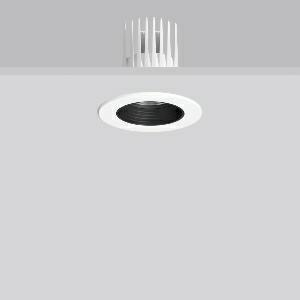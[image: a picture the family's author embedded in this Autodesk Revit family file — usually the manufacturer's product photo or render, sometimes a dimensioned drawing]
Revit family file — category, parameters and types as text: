
# Revit family: heledon_mini_e_901745_002_2_76_e601
name_source: partatom
category: Lighting Fixtures
units: mm (PartAtom-declared; Revit-internal decimal feet)

## family parameters
Cut with Voids When Loaded = No
Host = Face
Light Source = No
Part Type = Normal
Room Calculation Point = No
Round Connector Dimension = Use Diameter
Shared = No

## types (1)
- HELEDON mini E (1 x LED Modul 927, 1900 lm, 2700)
    Apparent Load = 20 VA
    Approval mark = CE
    CIE Flux Codes = 98 100 100 100 100
    Color Rendering = 92
    Color Temperature = 2700
    Default Elevation = 1800 mm
    Description = Series: HELEDON mini
Round recessed downlight. Housing: die-cast aluminium, powder-coated. Black plastic ring and recessed LED to prevent glare from the side. Optical assembly with lens made of plastic (polycarbonate) for the best homogeneous light distribution - can be changed without tools. Best colour rendering index Ra>90. Suitable for Recessed ceiling mounting. Installation without tools thanks to spring fastening system. Including separate LED converter with connecting cable 600 mm.High quality converter without flickering and stroboscopic effect. Through-wiring box (5 pole) available as accessory. The following accessories can be mounted without use of tools: interchangeable lenses, decorative glasses, honeycomb louvre, clear and frosted diffusers, white interchangeable plastic ring. 
Colour: traffic white, matt (RAL 9016)
Diameter: 124 mm
Height: 3 mm
Cut-out diameter: 114 mm
Recess height: 170 mm
Luminaire: recess height: 120 mm
Lamp: LED
Socket: without socket
Colour temperature: 2700K
Colour rendering index (CRI): 92
System power: 20 W
Rated luminous flux: 1900 lm
Luminous efficiency: 95 lm/W
Control gear: Converter, dimmable, DALI
Protection class: II
Type of protection: IP 20
    Height = 0 mm  [stored 0 ft]
    Lamp = 1 x LED Modul 927
    Lamp Light Flux = 1900 lm
    Lamp count = 1
    Length = 124 mm  [stored 0.406824 ft]
    Lifetime = 50000 h
    Luminous efficacy = 95 lm/W
    Manufacturer = RZB
    ModVariant = No
    Model = 901745.002.2.76
    Mounting Place = Ceiling
    Mounting Type = Recessed
    Number of Poles = 1
    OnlyDefault = Yes
    Power Factor = 1
    Product Name = HELEDON mini E
    Product group = Recessed downlights
    ProductGroupID = 402
    Protection Class = Protection class II
    Protection Degree = IP 20
    RLX_Detail_Level = 1
    RLX_Emergency_Light_Flux = 0 lm
    RLX_Emergency_Type = 0
    RLX_Emergency_Type_DB = No
    RlxData = <blob elided: 123969 chars, md5=f8286906>
    Socket = socket
    Standby Power = 0 W
    System Light Flux = 1900 lm
    System Power = 20 W
    Type Comments = Product without accessories
    Type Image = 901656.002.jpg
    URL = http://relux.com
    VarID = ---
    Voltage = 230 V
    Voltage Range = 220-240 V
    Weight = 0.00 kg
    Width = 0 mm  [stored 0 ft]

note: [stored X ft] marks values corroborated as IEEE doubles in the binary element streams (Revit-internal decimal feet)

## geometry (parser evidence)
native form markers: Blend x4, Sweep x11
no freeform markers — native parametric forms only
